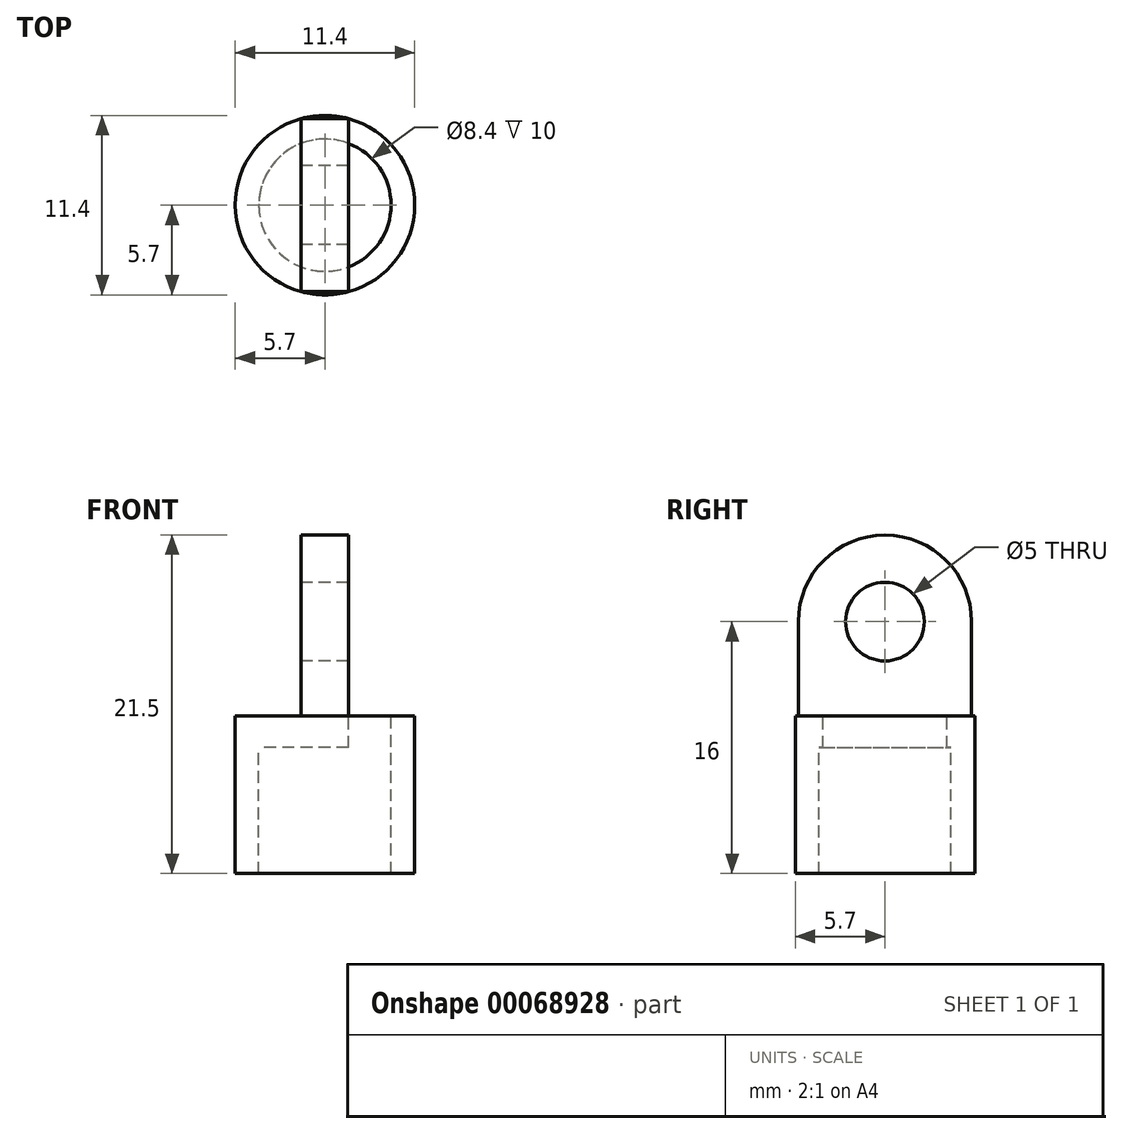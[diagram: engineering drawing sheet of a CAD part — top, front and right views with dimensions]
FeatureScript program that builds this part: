
annotation { "Feature Type Name" : "Feature", "Feature Type Description" : "" }
export const myFeature = defineFeature(function(context is Context, id is Id, definition is map)
    precondition{}
    {
        {
            var Q0;
            Q0=qCreatedBy(makeId("Right.planeOp"),FACE);
            var sketch = newSketch(context, id + "F0", { "sketchPlane" : qUnion([Q0])});
            skCircle(sketch, "E0", {"center": v(0, 0) * mm, "radius": 2.5 * mm});
            skCircle(sketch, "E1", {"center": v(0, 0) * mm, "radius": 5.5 * mm});
            skLineSegment(sketch, "E2", {"start": v(-5.5, 0) * mm, "end": v(-5.5, -6) * mm});
            skLineSegment(sketch, "E3", {"start": v(-5.5, -6) * mm, "end": v(5.5, -6) * mm});
            skLineSegment(sketch, "E4", {"start": v(5.5, -6) * mm, "end": v(5.5, 0) * mm});
            skLineSegment(sketch, "E5.top", {"start": v(-5.5, -8) * mm, "end": v(5.5, -8) * mm});
            skLineSegment(sketch, "E5.left", {"start": v(-5.5, -6) * mm, "end": v(-5.5, -8) * mm});
            skLineSegment(sketch, "E5.right", {"start": v(5.5, -6) * mm, "end": v(5.5, -8) * mm});
            skSolve(sketch);
        }
        {
            var Q0;
            Q0=makeQuery(id+"F0.imprint","IMPRINT",FACE,{"disambiguationData":[TD([[makeQuery(id+"F0.imprint","IMPRINT",EDGE,{"derivedFrom":sQuery(id+"F0.wireOp",EDGE,"E0")}),-1.0]])]});
            var Q1;
            {var subQ0=sQuery(id+"F0.wireOp",EDGE,"E2");Q1=makeQuery(id+"F0.imprint","IMPRINT",FACE,{"disambiguationData":[TD([[makeQuery(id+"F0.imprint","IMPRINT",EDGE,{"derivedFrom":subQ0}),1.0]])]});}
            extrude(context, id + "F1", {"entities" : qUnion([Q0, Q1]), "depth" : 1.5 * mm, "hasSecondDirection" : true, "secondDirectionOppositeDirection" : true, "secondDirectionDepth" : 1.5 * mm});
        }
        {
            var Q0;
            Q0=makeQuery(id+"F1.opExtrude","SWEPT_FACE",FACE,{"disambiguationData":[OSD([sQuery(id+"F0.wireOp",EDGE,"E3")])]});
            var sketch = newSketch(context, id + "F2", { "sketchPlane" : qUnion([Q0])});
            skCircle(sketch, "E6", {"center": v(0, 0) * mm, "radius": 4.2 * mm});
            skCircle(sketch, "E7", {"center": v(0, 0) * mm, "radius": 5.7 * mm});
            skSolve(sketch);
        }
        {
            var Q0;
            {var subQ0=sQuery(id+"F2.wireOp",EDGE,"E6");var subQ1=makeQuery(id+"F1.opExtrude","CAP_EDGE",EDGE,{"disambiguationData":[OSD([sQuery(id+"F0.wireOp",EDGE,"E3")])],"isStart":false});var subQ2=makeQuery(id+"F2.imprint","INTERSECT",VERTEX,{"disambiguationData":[OD(0.0)],"derivedFrom":[subQ1,subQ0]});Q0=makeQuery(id+"F2.imprint","IMPRINT",FACE,{"disambiguationData":[TD([[makeQuery(id+"F2.imprint","IMPRINT",EDGE,{"disambiguationData":[TD([[subQ2,1.0]])],"derivedFrom":subQ0}),1.0]])]});}
            var Q1;
            {var subQ0=sQuery(id+"F2.wireOp",EDGE,"E6");var subQ1=sQuery(id+"F0.wireOp",EDGE,"E3");var subQ2=makeQuery(id+"F1.opExtrude","CAP_EDGE",EDGE,{"disambiguationData":[OSD([subQ1])],"isStart":true});var subQ3=makeQuery(id+"F2.imprint","INTERSECT",VERTEX,{"disambiguationData":[OD(0.0)],"derivedFrom":[subQ2,subQ0]});Q1=makeQuery(id+"F2.imprint","IMPRINT",FACE,{"disambiguationData":[TD([[makeQuery(id+"F2.imprint","IMPRINT",EDGE,{"disambiguationData":[TD([[subQ3,1.0]])],"derivedFrom":subQ0}),1.0]])]});}
            var Q2;
            {var subQ0=sQuery(id+"F2.wireOp",EDGE,"E6");var subQ1=makeQuery(id+"F1.opExtrude","CAP_EDGE",EDGE,{"disambiguationData":[OSD([sQuery(id+"F0.wireOp",EDGE,"E3")])],"isStart":true});var subQ2=makeQuery(id+"F2.imprint","INTERSECT",VERTEX,{"disambiguationData":[OD(0.0)],"derivedFrom":[subQ1,subQ0]});Q2=makeQuery(id+"F2.imprint","IMPRINT",FACE,{"disambiguationData":[TD([[makeQuery(id+"F2.imprint","IMPRINT",EDGE,{"disambiguationData":[TD([[subQ2,-1.0]])],"derivedFrom":subQ0}),1.0]])]});}
            extrude(context, id + "F3", {"entities" : qUnion([Q0, Q1, Q2]), "operationType" : NewBodyOperationType.ADD, "depth" : 2 * mm});
        }
        {
            var Q0;
            Q0 = qSketchRegion(id + "F2", true);
            extrude(context, id + "F4", {"entities" : qUnion([Q0]), "operationType" : NewBodyOperationType.ADD, "depth" : 10 * mm});
        }
    });
